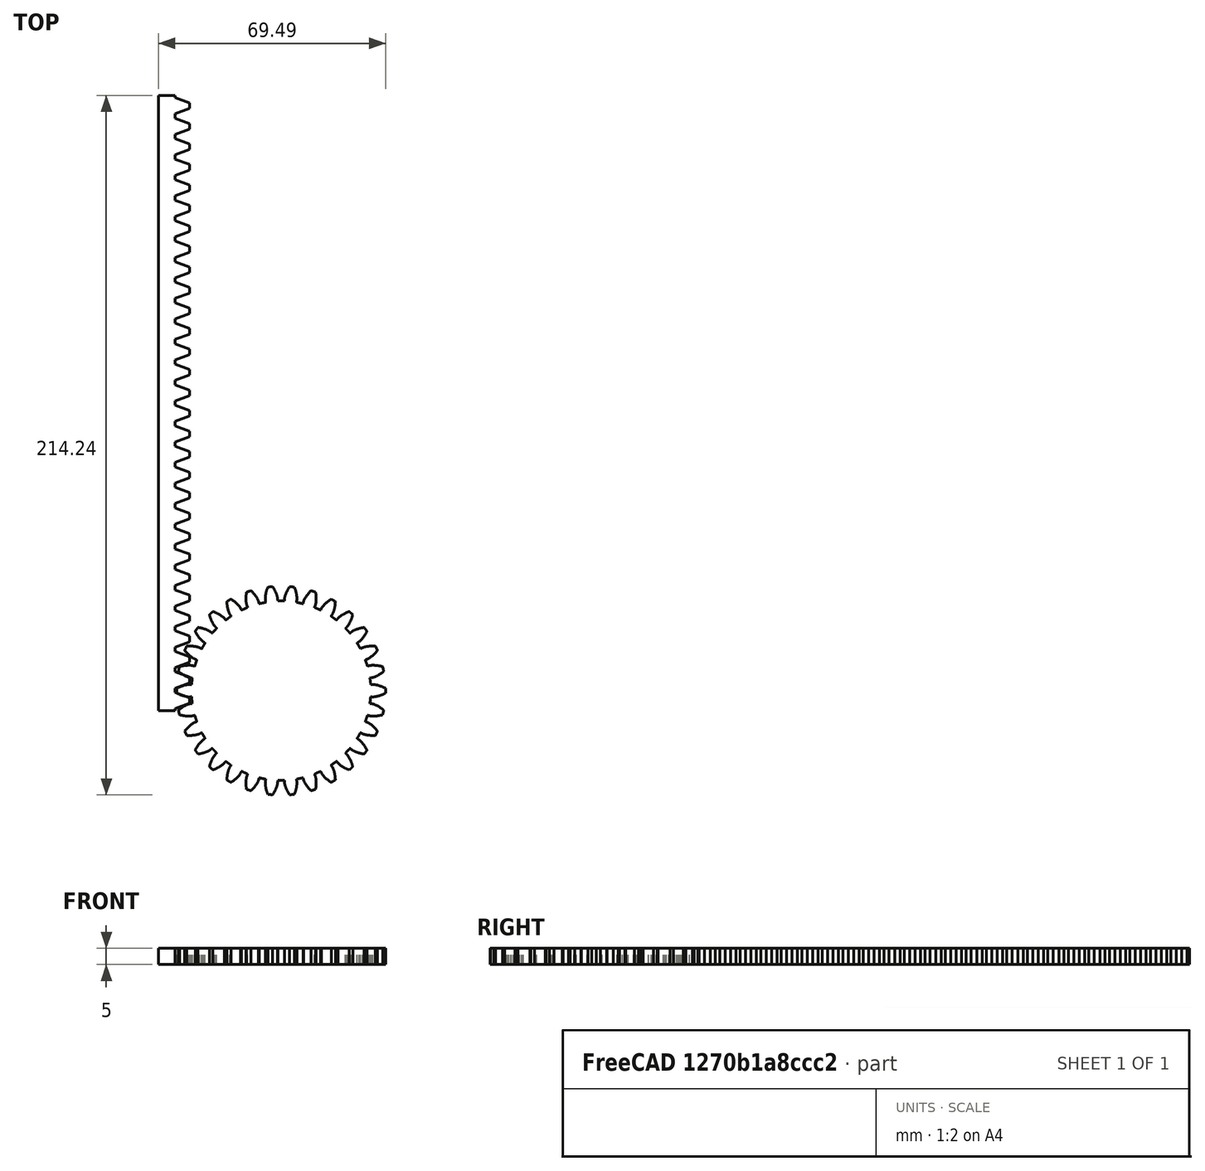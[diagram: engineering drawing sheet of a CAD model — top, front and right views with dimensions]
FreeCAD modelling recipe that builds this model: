
FCSTD DOCUMENT  (FreeCAD 0.21R33771 (Git))
Label: part1
License: All rights reserved
LicenseURL: http://en.wikipedia.org/wiki/All_rights_reserved
objects: App::Part×3, App::DocumentObjectGroup×3, App::Link×3, Part::FeaturePython×2, PartDesign::CoordinateSystem×1, App::FeaturePython×1
note: 3 computed .brp shape members not serialized (recipe doc carries the construction recipe); baked Part::Feature solids carry a one-line shape summary decoded from their .brp

FEATURE [Part::FeaturePython] InvoluteGear  # WARN: FeaturePython — macro-defined, semantics opaque (R4)
  AttacherType = Attacher::AttachEngine3D
  angular_backlash = 0
  backlash = 0
  beta = 0
  clearance = 0.25
  da = 64
  df = 55
  double_helix = false
  dw = 60
  head = 0
  head_fillet = 0
  height = 5
  module = 2
  numpoints = 20
  pressure_angle = 20
  properties_from_tool = false
  reversed_backlash = false
  root_fillet = 0
  shift = 0
  simple = false
  teeth = 30
  transverse_pitch = 6.28319
  traverse_module = 2
  undercut = false
  version = 1.2.0
  expr: angular_backlash = backlash / dw * 360 ° / pi
FEATURE [App::Part] Part  label="c-gear"
  Group = -> [InvoluteGear]
  Origin = -> Origin
FEATURE [Part::FeaturePython] InvoluteRack  # WARN: FeaturePython — macro-defined, semantics opaque (R4)
  AttacherType = Attacher::AttachEngine3D
  Placement = pos=(-30,-3,0) rot=(0,0,1;0rad)
  add_endings = true
  beta = 0
  clearance = 0.25
  double_helix = false
  head = 0
  head_fillet = 0
  height = 5
  module = 2
  pressure_angle = 20
  properties_from_tool = false
  root_fillet = 0
  simplified = false
  teeth = 30
  thickness = 5
  transverse_pitch = 6.28319
  version = 1.2.0
FEATURE [App::Part] Part001  label="sh-gear"
  Group = -> [InvoluteRack]
  Origin = -> Origin001
FEATURE [App::DocumentObjectGroup] Parts
  Group = -> [Part,Part001]
FEATURE [PartDesign::CoordinateSystem] LCS_Origin
  AttacherType = Attacher::AttachEngine3D
  MapMode = 2
  Support = -> [X_Axis002]
FEATURE [App::DocumentObjectGroup] Constraints
FEATURE [App::FeaturePython] Variables  # WARN: FeaturePython — macro-defined, semantics opaque (R4)
  Type = App::PropertyContainer
  move = 121
FEATURE [App::DocumentObjectGroup] Configurations
FEATURE [App::Link] c_gear  label="c-gear001"
  LinkPlacement = pos=(0,0,0) rot=(0,0,1;2.11185rad)
  LinkedObject = -> Part
  Placement = pos=(0,0,0) rot=(0,0,1;2.11185rad)
  expr: .Placement.Rotation.Angle = Variables.move
FEATURE [App::Link] sh_gear  label="sh-gear001"
  LinkPlacement = pos=(0,-63.3555,0) rot=(0,7,1;0rad)
  LinkedObject = -> Part001
  Placement = pos=(0,-63.3555,0) rot=(0,7,1;0rad)
  expr: .Placement.Base.y = -Variables.move * pi * 2 * 30 / 360
FEATURE [App::Link] sh_gear001  label="sh-gear002"
  LinkPlacement = pos=(0,63.3555,0) rot=(0,0,1;3.14159rad)
  LinkedObject = -> Part001
  Placement = pos=(0,63.3555,0) rot=(0,0,1;3.14159rad)
  expr: .Placement.Base.y = Variables.move * pi * 2 * 30 / 360
FEATURE [App::Part] Assembly
  AssemblyType = Part::Link
  Group = -> [LCS_Origin,Constraints,Variables,Configurations,c_gear,sh_gear,sh_gear001]
  Origin = -> Origin002
  Type = Assembly
